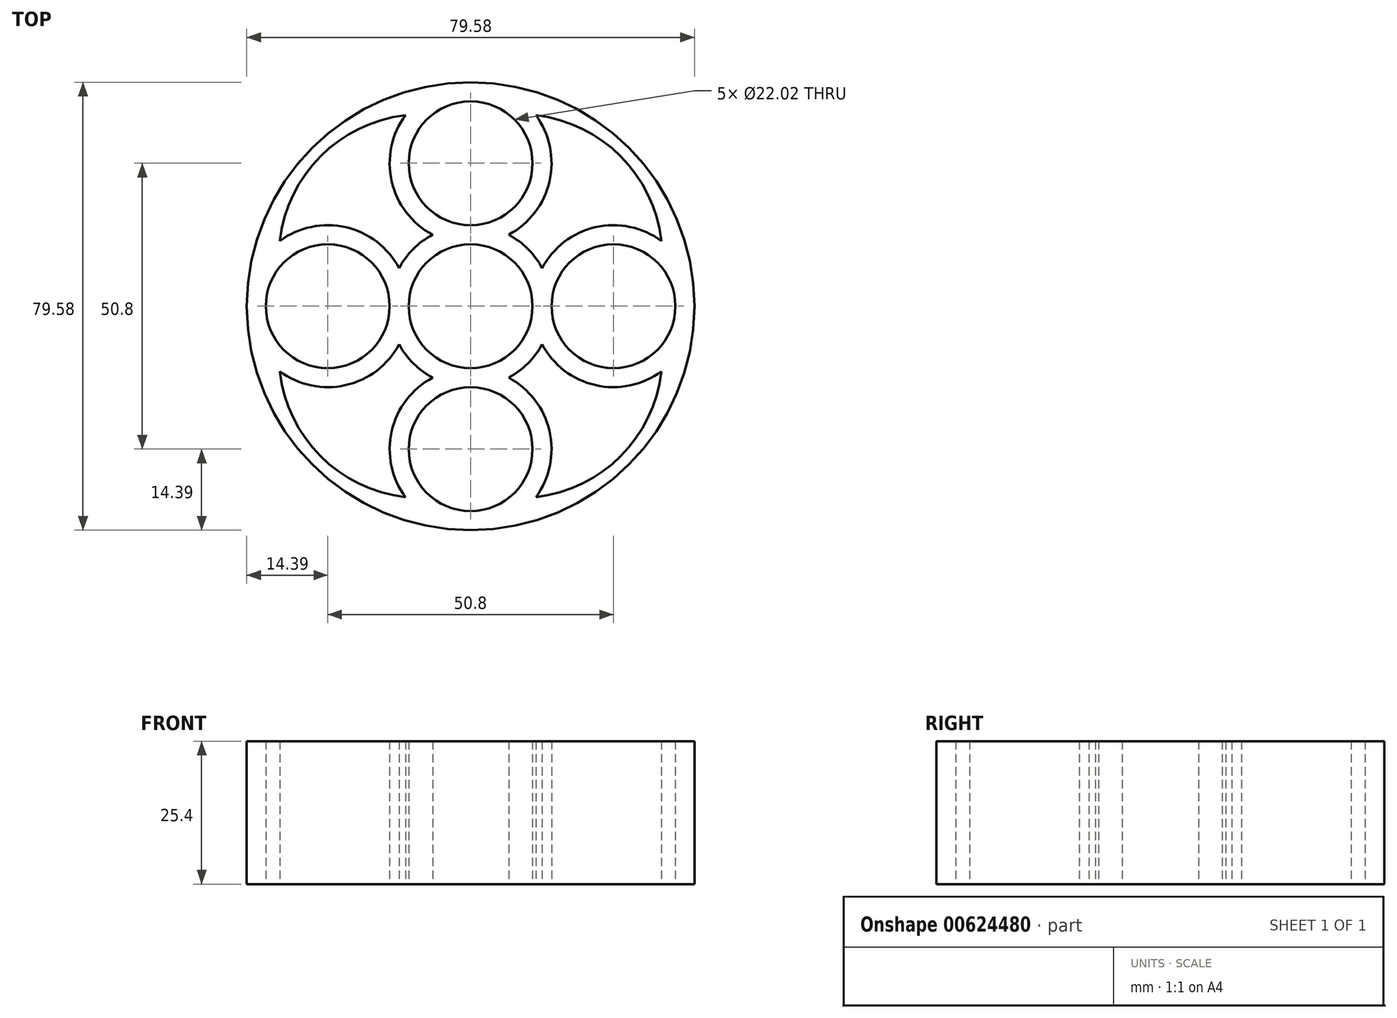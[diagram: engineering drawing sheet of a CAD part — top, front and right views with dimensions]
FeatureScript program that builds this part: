
annotation { "Feature Type Name" : "Feature", "Feature Type Description" : "" }
export const myFeature = defineFeature(function(context is Context, id is Id, definition is map)
    precondition{}
    {
        {
            var Q0;
            Q0=qCreatedBy(makeId("Top.planeOp"),FACE);
            var sketch = newSketch(context, id + "F0", { "sketchPlane" : qUnion([Q0])});
            skCircle(sketch, "E0", {"center": v(0, 25.4) * mm, "radius": 11.01 * mm});
            skCircle(sketch, "E1", {"center": v(-25.4, 0) * mm, "radius": 11.01 * mm});
            skCircle(sketch, "E2", {"center": v(0, -25.4) * mm, "radius": 11.01 * mm});
            skCircle(sketch, "E3", {"center": v(25.4, 0) * mm, "radius": 11.01 * mm});
            skCircle(sketch, "E4", {"center": v(0, 0) * mm, "radius": 11.01 * mm});
            skArc(sketch, "E5", {"start": v(-6.84, 34.03) * mm, "mid": v(-26.66, 26.66) * mm, "end": v(-34.03, 6.84) * mm});
            skArc(sketch, "E6", {"start": v(6.84, -34.03) * mm, "mid": v(26.66, -26.66) * mm, "end": v(34.03, -6.84) * mm});
            skArc(sketch, "E7", {"start": v(-34.03, -6.84) * mm, "mid": v(-26.66, -26.66) * mm, "end": v(-6.84, -34.03) * mm});
            skArc(sketch, "E8", {"start": v(34.03, 6.84) * mm, "mid": v(26.66, 26.66) * mm, "end": v(6.84, 34.03) * mm});
            skLineSegment(sketch, "E9", {"start": v(0, 0) * mm, "end": v(-25.4, 0) * mm});
            skLineSegment(sketch, "E10", {"start": v(0, 0) * mm, "end": v(0, 25.4) * mm});
            skLineSegment(sketch, "E11", {"start": v(0, 0) * mm, "end": v(25.4, 0) * mm});
            skLineSegment(sketch, "E12", {"start": v(0, -25.4) * mm, "end": v(0, 0) * mm});
            skCircle(sketch, "E13", {"center": v(0, 0) * mm, "radius": 14.39 * mm});
            skCircle(sketch, "E14", {"center": v(0, 0) * mm, "radius": 39.79 * mm});
            skCircle(sketch, "E15", {"center": v(-25.4, 0) * mm, "radius": 14.39 * mm});
            skCircle(sketch, "E16", {"center": v(0, 25.4) * mm, "radius": 14.39 * mm});
            skCircle(sketch, "E17", {"center": v(25.4, 0) * mm, "radius": 14.39 * mm});
            skCircle(sketch, "E18", {"center": v(0, -25.4) * mm, "radius": 14.39 * mm});
            skSolve(sketch);
        }
        {
            var Q0;
            {var subQ0=sQuery(id+"F0.wireOp",EDGE,"E11");var subQ1=sQuery(id+"F0.wireOp",EDGE,"E4");var subQ2=makeQuery(id+"F0.imprint","INTERSECT",VERTEX,{"derivedFrom":[subQ1,subQ0]});Q0=makeQuery(id+"F0.imprint","IMPRINT",FACE,{"disambiguationData":[TD([[makeQuery(id+"F0.imprint","IMPRINT",EDGE,{"disambiguationData":[TD([[subQ2,1.0]])],"derivedFrom":subQ1}),-1.0]])]});}
            var Q1;
            {var subQ3=sQuery(id+"F0.wireOp",EDGE,"tgp2MHNd-ltsj-E1Gy-TlMr-Zo4KxWsU06hy");Q1=makeQuery(id+"F0.imprint","IMPRINT",FACE,{"disambiguationData":[TD([[makeQuery(id+"F0.imprint","IMPRINT",EDGE,{"derivedFrom":subQ3}),-1.0]])]});}
            var Q2;
            {var subQ0=sQuery(id+"F0.wireOp",EDGE,"E10");var subQ1=sQuery(id+"F0.wireOp",EDGE,"E4");var subQ2=makeQuery(id+"F0.imprint","INTERSECT",VERTEX,{"derivedFrom":[subQ1,subQ0]});Q2=makeQuery(id+"F0.imprint","IMPRINT",FACE,{"disambiguationData":[TD([[makeQuery(id+"F0.imprint","IMPRINT",EDGE,{"disambiguationData":[TD([[subQ2,-1.0]])],"derivedFrom":subQ1}),-1.0]])]});}
            var Q3;
            {var subQ3=sQuery(id+"F0.wireOp",EDGE,"f4znQsOn-GAh7-7MiU-57vE-z4NArAqihcQ9");Q3=makeQuery(id+"F0.imprint","IMPRINT",FACE,{"disambiguationData":[TD([[makeQuery(id+"F0.imprint","IMPRINT",EDGE,{"derivedFrom":subQ3}),1.0]])]});}
            var Q4;
            {var subQ3=sQuery(id+"F0.wireOp",EDGE,"ydaiZZp2-0ypY-eHzZ-2PyJ-Qn3xicYvOAYB");Q4=makeQuery(id+"F0.imprint","IMPRINT",FACE,{"disambiguationData":[TD([[makeQuery(id+"F0.imprint","IMPRINT",EDGE,{"derivedFrom":subQ3}),-1.0]])]});}
            var Q5;
            {var subQ3=sQuery(id+"F0.wireOp",EDGE,"LW9KqEdj-jrCH-83YB-5hWu-STz3MlWoy6WS");Q5=makeQuery(id+"F0.imprint","IMPRINT",FACE,{"disambiguationData":[TD([[makeQuery(id+"F0.imprint","IMPRINT",EDGE,{"derivedFrom":subQ3}),1.0]])]});}
            var Q6;
            {var subQ3=sQuery(id+"F0.wireOp",EDGE,"73GzSDtE-wEZ4-a0qi-7Jov-GUcoDhd4TDFD");Q6=makeQuery(id+"F0.imprint","IMPRINT",FACE,{"disambiguationData":[TD([[makeQuery(id+"F0.imprint","IMPRINT",EDGE,{"derivedFrom":subQ3}),-1.0]])]});}
            var Q7;
            {var subQ3=sQuery(id+"F0.wireOp",EDGE,"FwocE1MT-7Wkx-19L4-LBzc-rtyO7ND7mUu5");Q7=makeQuery(id+"F0.imprint","IMPRINT",FACE,{"disambiguationData":[TD([[makeQuery(id+"F0.imprint","IMPRINT",EDGE,{"derivedFrom":subQ3}),1.0]])]});}
            var Q8;
            {var subQ3=sQuery(id+"F0.wireOp",EDGE,"nptUg5pC-Stug-CJhE-IECW-whuHZWUr2No6");Q8=makeQuery(id+"F0.imprint","IMPRINT",FACE,{"disambiguationData":[TD([[makeQuery(id+"F0.imprint","IMPRINT",EDGE,{"derivedFrom":subQ3}),-1.0]])]});}
            var Q9;
            {var subQ3=sQuery(id+"F0.wireOp",EDGE,"C8wvoh9j-nhv6-0o8d-D7NF-RznkwZHqPmpD");Q9=makeQuery(id+"F0.imprint","IMPRINT",FACE,{"disambiguationData":[TD([[makeQuery(id+"F0.imprint","IMPRINT",EDGE,{"derivedFrom":subQ3}),1.0]])]});}
            var Q10;
            {var subQ0=sQuery(id+"F0.wireOp",EDGE,"E10");var subQ1=sQuery(id+"F0.wireOp",EDGE,"E4");var subQ2=makeQuery(id+"F0.imprint","INTERSECT",VERTEX,{"derivedFrom":[subQ1,subQ0]});Q10=makeQuery(id+"F0.imprint","IMPRINT",FACE,{"disambiguationData":[TD([[makeQuery(id+"F0.imprint","IMPRINT",EDGE,{"disambiguationData":[TD([[subQ2,1.0]])],"derivedFrom":subQ1}),-1.0]])]});}
            var Q11;
            {var subQ0=sQuery(id+"F0.wireOp",EDGE,"E9");var subQ1=sQuery(id+"F0.wireOp",EDGE,"E4");var subQ2=makeQuery(id+"F0.imprint","INTERSECT",VERTEX,{"derivedFrom":[subQ1,subQ0]});Q11=makeQuery(id+"F0.imprint","IMPRINT",FACE,{"disambiguationData":[TD([[makeQuery(id+"F0.imprint","IMPRINT",EDGE,{"disambiguationData":[TD([[subQ2,-1.0]])],"derivedFrom":subQ1}),-1.0]])]});}
            var Q12;
            {var subQ0=sQuery(id+"F0.wireOp",EDGE,"E5");var subQ1=sQuery(id+"F0.wireOp",EDGE,"E0");var subQ2=makeQuery(id+"F0.imprint","INTERSECT",VERTEX,{"derivedFrom":[subQ1,subQ0]});Q12=makeQuery(id+"F0.imprint","IMPRINT",FACE,{"disambiguationData":[TD([[makeQuery(id+"F0.imprint","IMPRINT",EDGE,{"disambiguationData":[TD([[subQ2,1.0]])],"derivedFrom":subQ1}),-1.0]])]});}
            var Q13;
            {var subQ0=sQuery(id+"F0.wireOp",EDGE,"E8");var subQ1=sQuery(id+"F0.wireOp",EDGE,"E0");var subQ2=makeQuery(id+"F0.imprint","INTERSECT",VERTEX,{"derivedFrom":[subQ1,subQ0]});Q13=makeQuery(id+"F0.imprint","IMPRINT",FACE,{"disambiguationData":[TD([[makeQuery(id+"F0.imprint","IMPRINT",EDGE,{"disambiguationData":[TD([[subQ2,-1.0]])],"derivedFrom":subQ1}),-1.0]])]});}
            var Q14;
            {var subQ0=sQuery(id+"F0.wireOp",EDGE,"E17");var subQ1=sQuery(id+"F0.wireOp",EDGE,"E8");var subQ2=makeQuery(id+"F0.imprint","INTERSECT",VERTEX,{"derivedFrom":[subQ1,subQ0]});Q14=makeQuery(id+"F0.imprint","IMPRINT",FACE,{"disambiguationData":[TD([[makeQuery(id+"F0.imprint","IMPRINT",EDGE,{"disambiguationData":[TD([[subQ2,-1.0]])],"derivedFrom":subQ1}),-1.0]])]});}
            var Q15;
            {var subQ0=sQuery(id+"F0.wireOp",EDGE,"E8");var subQ1=sQuery(id+"F0.wireOp",EDGE,"E0");var subQ2=makeQuery(id+"F0.imprint","INTERSECT",VERTEX,{"derivedFrom":[subQ1,subQ0]});Q15=makeQuery(id+"F0.imprint","IMPRINT",FACE,{"disambiguationData":[TD([[makeQuery(id+"F0.imprint","IMPRINT",EDGE,{"disambiguationData":[TD([[subQ2,1.0]])],"derivedFrom":subQ0}),1.0]])]});}
            var Q16;
            {var subQ0=sQuery(id+"F0.wireOp",EDGE,"E5");var subQ1=sQuery(id+"F0.wireOp",EDGE,"E0");var subQ2=makeQuery(id+"F0.imprint","INTERSECT",VERTEX,{"derivedFrom":[subQ1,subQ0]});Q16=makeQuery(id+"F0.imprint","IMPRINT",FACE,{"disambiguationData":[TD([[makeQuery(id+"F0.imprint","IMPRINT",EDGE,{"disambiguationData":[TD([[subQ2,-1.0]])],"derivedFrom":subQ0}),1.0]])]});}
            var Q17;
            {var subQ0=sQuery(id+"F0.wireOp",EDGE,"E16");var subQ1=sQuery(id+"F0.wireOp",EDGE,"E5");var subQ2=makeQuery(id+"F0.imprint","INTERSECT",VERTEX,{"derivedFrom":[subQ1,subQ0]});Q17=makeQuery(id+"F0.imprint","IMPRINT",FACE,{"disambiguationData":[TD([[makeQuery(id+"F0.imprint","IMPRINT",EDGE,{"disambiguationData":[TD([[subQ2,-1.0]])],"derivedFrom":subQ1}),-1.0]])]});}
            var Q18;
            {var subQ0=sQuery(id+"F0.wireOp",EDGE,"E5");var subQ1=sQuery(id+"F0.wireOp",EDGE,"E1");var subQ2=makeQuery(id+"F0.imprint","INTERSECT",VERTEX,{"derivedFrom":[subQ1,subQ0]});Q18=makeQuery(id+"F0.imprint","IMPRINT",FACE,{"disambiguationData":[TD([[makeQuery(id+"F0.imprint","IMPRINT",EDGE,{"disambiguationData":[TD([[subQ2,-1.0]])],"derivedFrom":subQ1}),-1.0]])]});}
            var Q19;
            {var subQ0=sQuery(id+"F0.wireOp",EDGE,"E7");var subQ1=sQuery(id+"F0.wireOp",EDGE,"E1");var subQ2=makeQuery(id+"F0.imprint","INTERSECT",VERTEX,{"derivedFrom":[subQ1,subQ0]});Q19=makeQuery(id+"F0.imprint","IMPRINT",FACE,{"disambiguationData":[TD([[makeQuery(id+"F0.imprint","IMPRINT",EDGE,{"disambiguationData":[TD([[subQ2,1.0]])],"derivedFrom":subQ1}),-1.0]])]});}
            var Q20;
            {var subQ0=sQuery(id+"F0.wireOp",EDGE,"E7");var subQ1=sQuery(id+"F0.wireOp",EDGE,"E1");var subQ2=makeQuery(id+"F0.imprint","INTERSECT",VERTEX,{"derivedFrom":[subQ1,subQ0]});Q20=makeQuery(id+"F0.imprint","IMPRINT",FACE,{"disambiguationData":[TD([[makeQuery(id+"F0.imprint","IMPRINT",EDGE,{"disambiguationData":[TD([[subQ2,-1.0]])],"derivedFrom":subQ0}),1.0]])]});}
            var Q21;
            {var subQ0=sQuery(id+"F0.wireOp",EDGE,"E15");var subQ1=sQuery(id+"F0.wireOp",EDGE,"E7");var subQ2=makeQuery(id+"F0.imprint","INTERSECT",VERTEX,{"derivedFrom":[subQ1,subQ0]});Q21=makeQuery(id+"F0.imprint","IMPRINT",FACE,{"disambiguationData":[TD([[makeQuery(id+"F0.imprint","IMPRINT",EDGE,{"disambiguationData":[TD([[subQ2,-1.0]])],"derivedFrom":subQ1}),-1.0]])]});}
            var Q22;
            {var subQ0=sQuery(id+"F0.wireOp",EDGE,"E7");var subQ1=sQuery(id+"F0.wireOp",EDGE,"E2");var subQ2=makeQuery(id+"F0.imprint","INTERSECT",VERTEX,{"derivedFrom":[subQ1,subQ0]});Q22=makeQuery(id+"F0.imprint","IMPRINT",FACE,{"disambiguationData":[TD([[makeQuery(id+"F0.imprint","IMPRINT",EDGE,{"disambiguationData":[TD([[subQ2,1.0]])],"derivedFrom":subQ0}),1.0]])]});}
            var Q23;
            {var subQ0=sQuery(id+"F0.wireOp",EDGE,"E7");var subQ1=sQuery(id+"F0.wireOp",EDGE,"E2");var subQ2=makeQuery(id+"F0.imprint","INTERSECT",VERTEX,{"derivedFrom":[subQ1,subQ0]});Q23=makeQuery(id+"F0.imprint","IMPRINT",FACE,{"disambiguationData":[TD([[makeQuery(id+"F0.imprint","IMPRINT",EDGE,{"disambiguationData":[TD([[subQ2,-1.0]])],"derivedFrom":subQ1}),-1.0]])]});}
            var Q24;
            {var subQ0=sQuery(id+"F0.wireOp",EDGE,"E6");var subQ1=sQuery(id+"F0.wireOp",EDGE,"E2");var subQ2=makeQuery(id+"F0.imprint","INTERSECT",VERTEX,{"derivedFrom":[subQ1,subQ0]});Q24=makeQuery(id+"F0.imprint","IMPRINT",FACE,{"disambiguationData":[TD([[makeQuery(id+"F0.imprint","IMPRINT",EDGE,{"disambiguationData":[TD([[subQ2,1.0]])],"derivedFrom":subQ1}),-1.0]])]});}
            var Q25;
            {var subQ0=sQuery(id+"F0.wireOp",EDGE,"E6");var subQ1=sQuery(id+"F0.wireOp",EDGE,"E2");var subQ2=makeQuery(id+"F0.imprint","INTERSECT",VERTEX,{"derivedFrom":[subQ1,subQ0]});Q25=makeQuery(id+"F0.imprint","IMPRINT",FACE,{"disambiguationData":[TD([[makeQuery(id+"F0.imprint","IMPRINT",EDGE,{"disambiguationData":[TD([[subQ2,-1.0]])],"derivedFrom":subQ0}),1.0]])]});}
            var Q26;
            {var subQ0=sQuery(id+"F0.wireOp",EDGE,"E18");var subQ1=sQuery(id+"F0.wireOp",EDGE,"E6");var subQ2=makeQuery(id+"F0.imprint","INTERSECT",VERTEX,{"derivedFrom":[subQ1,subQ0]});Q26=makeQuery(id+"F0.imprint","IMPRINT",FACE,{"disambiguationData":[TD([[makeQuery(id+"F0.imprint","IMPRINT",EDGE,{"disambiguationData":[TD([[subQ2,-1.0]])],"derivedFrom":subQ1}),-1.0]])]});}
            var Q27;
            {var subQ0=sQuery(id+"F0.wireOp",EDGE,"E6");var subQ1=sQuery(id+"F0.wireOp",EDGE,"E3");var subQ2=makeQuery(id+"F0.imprint","INTERSECT",VERTEX,{"derivedFrom":[subQ1,subQ0]});Q27=makeQuery(id+"F0.imprint","IMPRINT",FACE,{"disambiguationData":[TD([[makeQuery(id+"F0.imprint","IMPRINT",EDGE,{"disambiguationData":[TD([[subQ2,-1.0]])],"derivedFrom":subQ1}),-1.0]])]});}
            var Q28;
            {var subQ0=sQuery(id+"F0.wireOp",EDGE,"E17");var subQ1=sQuery(id+"F0.wireOp",EDGE,"E14");var subQ2=makeQuery(id+"F0.imprint","INTERSECT",VERTEX,{"disambiguationData":[OD(0.0)],"derivedFrom":[subQ1,subQ0]});Q28=makeQuery(id+"F0.imprint","IMPRINT",FACE,{"disambiguationData":[TD([[makeQuery(id+"F0.imprint","IMPRINT",EDGE,{"disambiguationData":[TD([[subQ2,1.0]])],"derivedFrom":subQ1}),-1.0]])]});}
            var Q29;
            {var subQ0=sQuery(id+"F0.wireOp",EDGE,"E8");var subQ1=sQuery(id+"F0.wireOp",EDGE,"E3");var subQ2=makeQuery(id+"F0.imprint","INTERSECT",VERTEX,{"derivedFrom":[subQ1,subQ0]});Q29=makeQuery(id+"F0.imprint","IMPRINT",FACE,{"disambiguationData":[TD([[makeQuery(id+"F0.imprint","IMPRINT",EDGE,{"disambiguationData":[TD([[subQ2,1.0]])],"derivedFrom":subQ1}),-1.0]])]});}
            var Q30;
            {var subQ0=sQuery(id+"F0.wireOp",EDGE,"E8");var subQ1=sQuery(id+"F0.wireOp",EDGE,"E3");var subQ2=makeQuery(id+"F0.imprint","INTERSECT",VERTEX,{"derivedFrom":[subQ1,subQ0]});Q30=makeQuery(id+"F0.imprint","IMPRINT",FACE,{"disambiguationData":[TD([[makeQuery(id+"F0.imprint","IMPRINT",EDGE,{"disambiguationData":[TD([[subQ2,-1.0]])],"derivedFrom":subQ0}),1.0]])]});}
            var Q31;
            {var subQ0=sQuery(id+"F0.wireOp",EDGE,"E13");var subQ3=sQuery(id+"F0.wireOp",EDGE,"E17");var subQ5=makeQuery(id+"F0.imprint","INTERSECT",VERTEX,{"disambiguationData":[OD(0.0)],"derivedFrom":[subQ0,subQ3]});Q31=makeQuery(id+"F0.imprint","IMPRINT",FACE,{"disambiguationData":[TD([[makeQuery(id+"F0.imprint","IMPRINT",EDGE,{"disambiguationData":[TD([[subQ5,1.0]])],"derivedFrom":subQ0}),1.0]])]});}
            var Q32;
            {var subQ0=sQuery(id+"F0.wireOp",EDGE,"E13");var subQ3=sQuery(id+"F0.wireOp",EDGE,"E17");var subQ5=makeQuery(id+"F0.imprint","INTERSECT",VERTEX,{"disambiguationData":[OD(1.0)],"derivedFrom":[subQ0,subQ3]});Q32=makeQuery(id+"F0.imprint","IMPRINT",FACE,{"disambiguationData":[TD([[makeQuery(id+"F0.imprint","IMPRINT",EDGE,{"disambiguationData":[TD([[subQ5,-1.0]])],"derivedFrom":subQ0}),1.0]])]});}
            var Q33;
            {var subQ0=sQuery(id+"F0.wireOp",EDGE,"E6");var subQ1=sQuery(id+"F0.wireOp",EDGE,"E3");var subQ2=makeQuery(id+"F0.imprint","INTERSECT",VERTEX,{"derivedFrom":[subQ1,subQ0]});Q33=makeQuery(id+"F0.imprint","IMPRINT",FACE,{"disambiguationData":[TD([[makeQuery(id+"F0.imprint","IMPRINT",EDGE,{"disambiguationData":[TD([[subQ2,1.0]])],"derivedFrom":subQ0}),1.0]])]});}
            var Q34;
            {var subQ0=sQuery(id+"F0.wireOp",EDGE,"E13");var subQ3=sQuery(id+"F0.wireOp",EDGE,"E18");var subQ5=makeQuery(id+"F0.imprint","INTERSECT",VERTEX,{"disambiguationData":[OD(1.0)],"derivedFrom":[subQ0,subQ3]});Q34=makeQuery(id+"F0.imprint","IMPRINT",FACE,{"disambiguationData":[TD([[makeQuery(id+"F0.imprint","IMPRINT",EDGE,{"disambiguationData":[TD([[subQ5,1.0]])],"derivedFrom":subQ0}),1.0]])]});}
            var Q35;
            {var subQ0=sQuery(id+"F0.wireOp",EDGE,"E13");var subQ3=sQuery(id+"F0.wireOp",EDGE,"E18");var subQ5=makeQuery(id+"F0.imprint","INTERSECT",VERTEX,{"disambiguationData":[OD(0.0)],"derivedFrom":[subQ0,subQ3]});Q35=makeQuery(id+"F0.imprint","IMPRINT",FACE,{"disambiguationData":[TD([[makeQuery(id+"F0.imprint","IMPRINT",EDGE,{"disambiguationData":[TD([[subQ5,-1.0]])],"derivedFrom":subQ0}),1.0]])]});}
            var Q36;
            {var subQ0=sQuery(id+"F0.wireOp",EDGE,"E13");var subQ3=sQuery(id+"F0.wireOp",EDGE,"E15");var subQ5=makeQuery(id+"F0.imprint","INTERSECT",VERTEX,{"disambiguationData":[OD(1.0)],"derivedFrom":[subQ0,subQ3]});Q36=makeQuery(id+"F0.imprint","IMPRINT",FACE,{"disambiguationData":[TD([[makeQuery(id+"F0.imprint","IMPRINT",EDGE,{"disambiguationData":[TD([[subQ5,1.0]])],"derivedFrom":subQ0}),1.0]])]});}
            var Q37;
            {var subQ0=sQuery(id+"F0.wireOp",EDGE,"E13");var subQ3=sQuery(id+"F0.wireOp",EDGE,"E15");var subQ5=makeQuery(id+"F0.imprint","INTERSECT",VERTEX,{"disambiguationData":[OD(0.0)],"derivedFrom":[subQ0,subQ3]});Q37=makeQuery(id+"F0.imprint","IMPRINT",FACE,{"disambiguationData":[TD([[makeQuery(id+"F0.imprint","IMPRINT",EDGE,{"disambiguationData":[TD([[subQ5,-1.0]])],"derivedFrom":subQ0}),1.0]])]});}
            var Q38;
            {var subQ0=sQuery(id+"F0.wireOp",EDGE,"E13");var subQ3=sQuery(id+"F0.wireOp",EDGE,"E16");var subQ5=makeQuery(id+"F0.imprint","INTERSECT",VERTEX,{"disambiguationData":[OD(1.0)],"derivedFrom":[subQ0,subQ3]});Q38=makeQuery(id+"F0.imprint","IMPRINT",FACE,{"disambiguationData":[TD([[makeQuery(id+"F0.imprint","IMPRINT",EDGE,{"disambiguationData":[TD([[subQ5,1.0]])],"derivedFrom":subQ0}),1.0]])]});}
            var Q39;
            {var subQ0=sQuery(id+"F0.wireOp",EDGE,"E13");var subQ3=sQuery(id+"F0.wireOp",EDGE,"E16");var subQ5=makeQuery(id+"F0.imprint","INTERSECT",VERTEX,{"disambiguationData":[OD(0.0)],"derivedFrom":[subQ0,subQ3]});Q39=makeQuery(id+"F0.imprint","IMPRINT",FACE,{"disambiguationData":[TD([[makeQuery(id+"F0.imprint","IMPRINT",EDGE,{"disambiguationData":[TD([[subQ5,-1.0]])],"derivedFrom":subQ0}),1.0]])]});}
            var Q40;
            {var subQ0=sQuery(id+"F0.wireOp",EDGE,"E5");var subQ1=sQuery(id+"F0.wireOp",EDGE,"E1");var subQ2=makeQuery(id+"F0.imprint","INTERSECT",VERTEX,{"derivedFrom":[subQ1,subQ0]});Q40=makeQuery(id+"F0.imprint","IMPRINT",FACE,{"disambiguationData":[TD([[makeQuery(id+"F0.imprint","IMPRINT",EDGE,{"disambiguationData":[TD([[subQ2,1.0]])],"derivedFrom":subQ0}),1.0]])]});}
            extrude(context, id + "F1", {"entities" : qUnion([Q0, Q1, Q2, Q3, Q4, Q5, Q6, Q7, Q8, Q9, Q10, Q11, Q12, Q13, Q14, Q15, Q16, Q17, Q18, Q19, Q20, Q21, Q22, Q23, Q24, Q25, Q26, Q27, Q28, Q29, Q30, Q31, Q32, Q33, Q34, Q35, Q36, Q37, Q38, Q39, Q40]), "depth" : 25.4 * mm, "offsetDistance" : 25.4 * mm});
        }
    });
